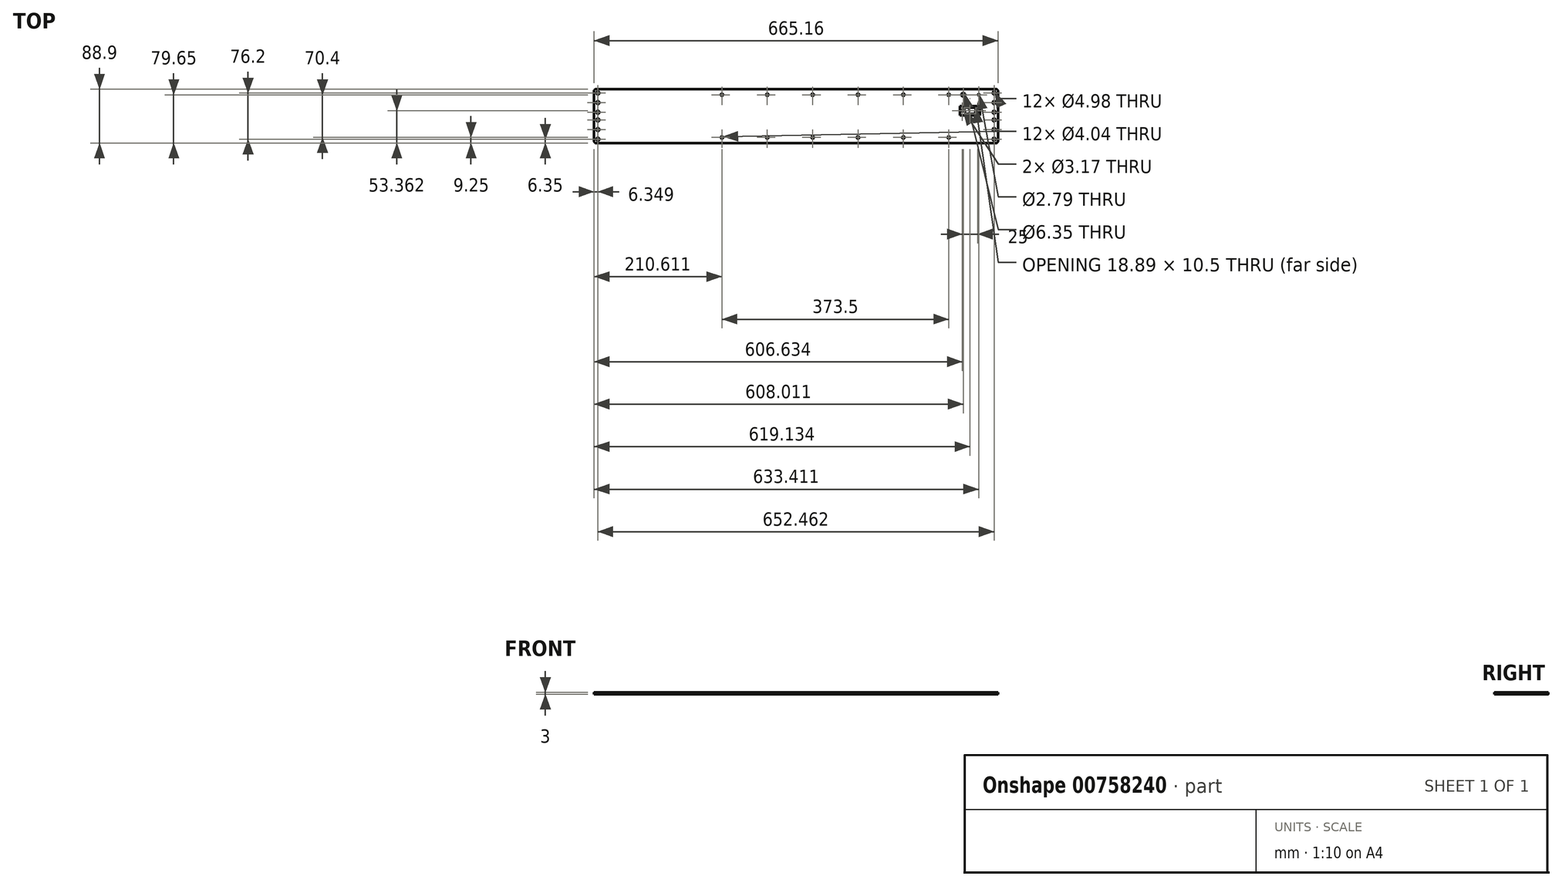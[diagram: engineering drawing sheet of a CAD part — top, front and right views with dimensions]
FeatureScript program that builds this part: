
annotation { "Feature Type Name" : "Feature", "Feature Type Description" : "" }
export const myFeature = defineFeature(function(context is Context, id is Id, definition is map)
    precondition{}
    {
        {
            var Q0;
            Q0=qCreatedBy(makeId("Top.planeOp"),FACE);
            var sketch = newSketch(context, id + "F0", { "sketchPlane" : qUnion([Q0])});
            skLineSegment(sketch, "E0.bottom", {"start": v(-329.4, 44.45) * mm, "end": v(329.4, 44.45) * mm});
            skLineSegment(sketch, "E0.top", {"start": v(-329.4, -44.45) * mm, "end": v(329.4, -44.45) * mm});
            skLineSegment(sketch, "E0.left", {"start": v(-332.58, 41.28) * mm, "end": v(-332.58, -41.28) * mm});
            skLineSegment(sketch, "E0.right", {"start": v(332.58, 41.28) * mm, "end": v(332.58, -41.28) * mm});
            skPoint(sketch, "E1", {"position": v(0, 0) * mm});
            skPoint(sketch, "E2", {"position": v(0, -44.45) * mm});
            skPoint(sketch, "E3", {"position": v(332.58, 0) * mm});
            skLineSegment(sketch, "E4", {"start": v(332.58, 0) * mm, "end": v(-332.58, 0) * mm, "construction": true});
            skLineSegment(sketch, "E5", {"start": v(326.23, 44.45) * mm, "end": v(326.23, -44.45) * mm, "construction": true});
            skLineSegment(sketch, "E6", {"start": v(-326.23, 44.45) * mm, "end": v(-326.23, -44.45) * mm, "construction": true});
            skCircle(sketch, "E7", {"center": v(-326.23, 6.35) * mm, "radius": 2.49 * mm});
            skCircle(sketch, "E8", {"center": v(-326.23, -6.35) * mm, "radius": 2.49 * mm});
            skCircle(sketch, "E9", {"center": v(-326.23, -22.23) * mm, "radius": 2.49 * mm});
            skCircle(sketch, "E10", {"center": v(-326.23, -38.1) * mm, "radius": 2.49 * mm});
            skCircle(sketch, "E11", {"center": v(-326.23, 22.22) * mm, "radius": 2.49 * mm});
            skCircle(sketch, "E12", {"center": v(-326.23, 38.1) * mm, "radius": 2.49 * mm});
            skCircle(sketch, "E13", {"center": v(326.23, 6.35) * mm, "radius": 2.49 * mm});
            skCircle(sketch, "E14", {"center": v(326.23, 22.22) * mm, "radius": 2.49 * mm});
            skCircle(sketch, "E15", {"center": v(326.23, 38.1) * mm, "radius": 2.49 * mm});
            skCircle(sketch, "E16", {"center": v(326.23, -6.35) * mm, "radius": 2.49 * mm});
            skCircle(sketch, "E17", {"center": v(326.23, -22.23) * mm, "radius": 2.49 * mm});
            skCircle(sketch, "E18", {"center": v(326.23, -38.1) * mm, "radius": 2.49 * mm});
            skLineSegment(sketch, "E19", {"start": v(251.53, 44.45) * mm, "end": v(251.53, -44.45) * mm, "construction": true});
            skLineSegment(sketch, "E20", {"start": v(176.83, 44.45) * mm, "end": v(176.83, -44.45) * mm, "construction": true});
            skLineSegment(sketch, "E21", {"start": v(102.13, 44.45) * mm, "end": v(102.13, -44.45) * mm, "construction": true});
            skLineSegment(sketch, "E22", {"start": v(27.43, 44.45) * mm, "end": v(27.43, -44.45) * mm, "construction": true});
            skLineSegment(sketch, "E23", {"start": v(-47.27, 44.45) * mm, "end": v(-47.27, -44.45) * mm, "construction": true});
            skLineSegment(sketch, "E24", {"start": v(-121.97, 44.45) * mm, "end": v(-121.97, -44.45) * mm, "construction": true});
            skLineSegment(sketch, "E25", {"start": v(-332.58, 35.2) * mm, "end": v(332.58, 35.2) * mm, "construction": true});
            skLineSegment(sketch, "E26", {"start": v(332.58, -35.2) * mm, "end": v(-326.23, -35.2) * mm, "construction": true});
            skCircle(sketch, "E27", {"center": v(-121.97, 35.2) * mm, "radius": 2.02 * mm});
            skCircle(sketch, "E28", {"center": v(-121.97, -35.2) * mm, "radius": 2.02 * mm});
            skCircle(sketch, "E29", {"center": v(-47.27, 35.2) * mm, "radius": 2.02 * mm});
            skCircle(sketch, "E30", {"center": v(-47.27, -35.2) * mm, "radius": 2.02 * mm});
            skCircle(sketch, "E31", {"center": v(27.43, 35.2) * mm, "radius": 2.02 * mm});
            skCircle(sketch, "E32", {"center": v(27.43, -35.2) * mm, "radius": 2.02 * mm});
            skCircle(sketch, "E33", {"center": v(102.13, 35.2) * mm, "radius": 2.02 * mm});
            skCircle(sketch, "E34", {"center": v(102.13, -35.2) * mm, "radius": 2.02 * mm});
            skCircle(sketch, "E35", {"center": v(176.83, 35.2) * mm, "radius": 2.02 * mm});
            skCircle(sketch, "E36", {"center": v(176.83, -35.2) * mm, "radius": 2.02 * mm});
            skCircle(sketch, "E37", {"center": v(251.53, 35.2) * mm, "radius": 2.02 * mm});
            skCircle(sketch, "E38", {"center": v(251.53, -35.2) * mm, "radius": 2.02 * mm});
            skPoint(sketch, "E39.visualSharp", {"position": v(-332.58, 44.45) * mm});
            skArc(sketch, "E39.filletArc", {"start": v(-329.4, 44.45) * mm, "mid": v(-331.65, 43.52) * mm, "end": v(-332.58, 41.28) * mm});
            skPoint(sketch, "E40.visualSharp", {"position": v(-332.58, -44.45) * mm});
            skArc(sketch, "E40.filletArc", {"start": v(-332.58, -41.28) * mm, "mid": v(-331.65, -43.52) * mm, "end": v(-329.4, -44.45) * mm});
            skPoint(sketch, "E41.visualSharp", {"position": v(332.58, 44.45) * mm});
            skArc(sketch, "E41.filletArc", {"start": v(332.58, 41.28) * mm, "mid": v(331.65, 43.52) * mm, "end": v(329.4, 44.45) * mm});
            skPoint(sketch, "E42.visualSharp", {"position": v(332.58, -44.45) * mm});
            skArc(sketch, "E42.filletArc", {"start": v(329.4, -44.45) * mm, "mid": v(331.65, -43.52) * mm, "end": v(332.58, -41.28) * mm});
            skCircle(sketch, "E43", {"center": v(300.83, 35.2) * mm, "radius": 1.4 * mm});
            skCircle(sketch, "E44", {"center": v(275.43, 35.2) * mm, "radius": 3.18 * mm});
            skSolve(sketch);
        }
        {
            var Q0;
            Q0=makeQuery(id+"F0.imprint","IMPRINT",FACE,{"disambiguationData":[TD([[makeQuery(id+"F0.imprint","IMPRINT",EDGE,{"derivedFrom":sQuery(id+"F0.wireOp",EDGE,"E0.bottom")}),-1.0]])]});
            var sketch = newSketch(context, id + "F1", { "sketchPlane" : qUnion([Q0])});
            skPoint(sketch, "E45", {"position": v(286.55, 8.91) * mm});
            skLineSegment(sketch, "E46.bottom", {"start": v(279.99, 14.16) * mm, "end": v(293.12, 14.16) * mm});
            skLineSegment(sketch, "E46.top", {"start": v(280.82, 3.66) * mm, "end": v(292.29, 3.66) * mm});
            skPoint(sketch, "E47", {"position": v(296.55, 8.91) * mm});
            skPoint(sketch, "E48", {"position": v(286.55, 14.16) * mm});
            skLineSegment(sketch, "E49", {"start": v(277.15, 10.78) * mm, "end": v(277.99, 6.04) * mm});
            skLineSegment(sketch, "E50", {"start": v(295.96, 10.78) * mm, "end": v(295.12, 6.04) * mm});
            skPoint(sketch, "E51.orphan", {"position": v(296.55, 3.66) * mm});
            skPoint(sketch, "E52.visualSharp", {"position": v(276.55, 14.16) * mm});
            skArc(sketch, "E52.filletArc", {"start": v(279.99, 14.16) * mm, "mid": v(277.78, 13.13) * mm, "end": v(277.15, 10.78) * mm});
            skPoint(sketch, "E53.visualSharp", {"position": v(296.55, 14.16) * mm});
            skArc(sketch, "E53.filletArc", {"start": v(295.96, 10.78) * mm, "mid": v(295.33, 13.13) * mm, "end": v(293.12, 14.16) * mm});
            skPoint(sketch, "E54.visualSharp", {"position": v(294.7, 3.66) * mm});
            skArc(sketch, "E54.filletArc", {"start": v(292.29, 3.66) * mm, "mid": v(294.14, 4.34) * mm, "end": v(295.12, 6.04) * mm});
            skPoint(sketch, "E55.visualSharp", {"position": v(278.4, 3.66) * mm});
            skArc(sketch, "E55.filletArc", {"start": v(277.99, 6.04) * mm, "mid": v(278.97, 4.34) * mm, "end": v(280.82, 3.66) * mm});
            skCircle(sketch, "E56", {"center": v(274.05, 8.91) * mm, "radius": 1.59 * mm});
            skCircle(sketch, "E57", {"center": v(299.05, 8.91) * mm, "radius": 1.59 * mm});
            skSolve(sketch);
        }
        {
            var Q0;
            Q0 = qSketchRegion(id + "F0", true);
            extrude(context, id + "F2", {"entities" : qUnion([Q0]), "depth" : 3 * mm, "offsetDistance" : 25.4 * mm});
        }
        {
            var Q0;
            Q0 = qSketchRegion(id + "F1", true);
            extrude(context, id + "F3", {"entities" : qUnion([Q0]), "operationType" : NewBodyOperationType.REMOVE, "endBound" : BoundingType.THROUGH_ALL, "depth" : 25.4 * mm, "offsetDistance" : 25.4 * mm});
        }
        {
            var Q0;
            Q0=makeQuery(id+"F2.opExtrude","CAP_FACE",FACE,{"disambiguationData":[OSD([sQuery(id+"F0.wireOp",EDGE,"E0.bottom"),sQuery(id+"F0.wireOp",EDGE,"E0.top"),sQuery(id+"F0.wireOp",EDGE,"E0.left"),sQuery(id+"F0.wireOp",EDGE,"E0.right"),sQuery(id+"F0.wireOp",EDGE,"E7"),sQuery(id+"F0.wireOp",EDGE,"E8"),sQuery(id+"F0.wireOp",EDGE,"E9"),sQuery(id+"F0.wireOp",EDGE,"E10"),sQuery(id+"F0.wireOp",EDGE,"E11"),sQuery(id+"F0.wireOp",EDGE,"E12"),sQuery(id+"F0.wireOp",EDGE,"E13"),sQuery(id+"F0.wireOp",EDGE,"E14"),sQuery(id+"F0.wireOp",EDGE,"E15"),sQuery(id+"F0.wireOp",EDGE,"E16"),sQuery(id+"F0.wireOp",EDGE,"E17"),sQuery(id+"F0.wireOp",EDGE,"E18"),sQuery(id+"F0.wireOp",EDGE,"E27"),sQuery(id+"F0.wireOp",EDGE,"E28"),sQuery(id+"F0.wireOp",EDGE,"E29"),sQuery(id+"F0.wireOp",EDGE,"E30"),sQuery(id+"F0.wireOp",EDGE,"E31"),sQuery(id+"F0.wireOp",EDGE,"E32"),sQuery(id+"F0.wireOp",EDGE,"E33"),sQuery(id+"F0.wireOp",EDGE,"E34"),sQuery(id+"F0.wireOp",EDGE,"E35"),sQuery(id+"F0.wireOp",EDGE,"E36"),sQuery(id+"F0.wireOp",EDGE,"E37"),sQuery(id+"F0.wireOp",EDGE,"E38"),sQuery(id+"F0.wireOp",EDGE,"E39.filletArc"),sQuery(id+"F0.wireOp",EDGE,"E40.filletArc"),sQuery(id+"F0.wireOp",EDGE,"E41.filletArc"),sQuery(id+"F0.wireOp",EDGE,"E42.filletArc")])],"isStart":false});
            var sketch = newSketch(context, id + "F4", { "sketchPlane" : qUnion([Q0])});
            skPoint(sketch, "E58", {"position": v(274.05, 8.91) * mm});
            skPoint(sketch, "E59", {"position": v(299.05, 8.91) * mm});
            skPoint(sketch, "E60", {"position": v(286.55, 14.16) * mm});
            skLineSegment(sketch, "E61", {"start": v(286.55, 14.16) * mm, "end": v(286.55, 3.66) * mm, "construction": true});
            skLineSegment(sketch, "E62", {"start": v(274.05, 8.91) * mm, "end": v(299.05, 8.91) * mm, "construction": true});
            skLineSegment(sketch, "E63.bottom", {"start": v(270.04, 16.53) * mm, "end": v(303.06, 16.53) * mm});
            skLineSegment(sketch, "E63.top", {"start": v(270.04, 1.3) * mm, "end": v(303.06, 1.3) * mm});
            skLineSegment(sketch, "E63.left", {"start": v(270.04, 16.53) * mm, "end": v(270.04, 1.3) * mm});
            skLineSegment(sketch, "E63.right", {"start": v(303.06, 16.53) * mm, "end": v(303.06, 1.3) * mm});
            skPoint(sketch, "E64", {"position": v(286.55, 16.53) * mm});
            skPoint(sketch, "E65", {"position": v(270.04, 8.91) * mm});
            skSolve(sketch);
        }
        {
            var Q0;
            Q0 = qSketchRegion(id + "F4", true);
            extrude(context, id + "F5", {"entities" : qUnion([Q0]), "operationType" : NewBodyOperationType.REMOVE, "oppositeDirection" : true, "depth" : 1.41 * mm, "offsetDistance" : 25.4 * mm});
        }
    });
